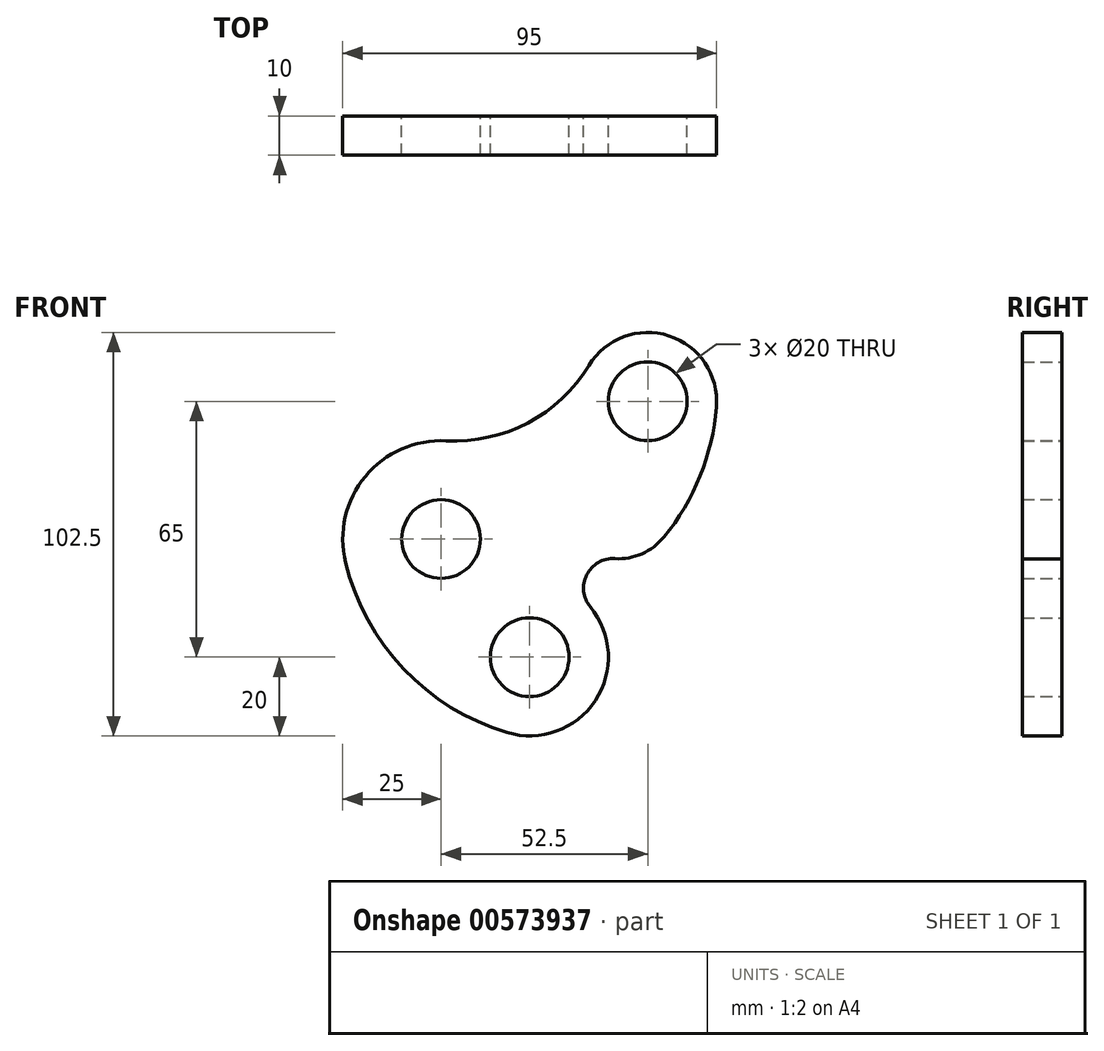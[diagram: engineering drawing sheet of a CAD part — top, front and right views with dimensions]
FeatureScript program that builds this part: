
annotation { "Feature Type Name" : "Feature", "Feature Type Description" : "" }
export const myFeature = defineFeature(function(context is Context, id is Id, definition is map)
    precondition{}
    {
        {
            var Q0;
            Q0=qCreatedBy(makeId("Front.planeOp"),FACE);
            var sketch = newSketch(context, id + "F0", { "sketchPlane" : qUnion([Q0])});
            skCircle(sketch, "E0", {"center": v(0, 0) * mm, "radius": 10 * mm});
            skCircle(sketch, "E1", {"center": v(22.5, -30) * mm, "radius": 10 * mm});
            skCircle(sketch, "E2", {"center": v(52.5, 35) * mm, "radius": 10 * mm});
            skArc(sketch, "E3", {"start": v(1.3, 24.97) * mm, "mid": v(-19.26, 15.94) * mm, "end": v(-24.28, -5.94) * mm});
            skArc(sketch, "E4", {"start": v(16.75, -49.16) * mm, "mid": v(39.17, -41.05) * mm, "end": v(37.9, -17.24) * mm});
            skArc(sketch, "E5", {"start": v(1.3, 24.97) * mm, "mid": v(22.07, 29.54) * mm, "end": v(37.55, 44.1) * mm});
            skArc(sketch, "E6", {"start": v(56.62, 0.51) * mm, "mid": v(65.8, 16.03) * mm, "end": v(69.94, 33.58) * mm});
            skArc(sketch, "E7", {"start": v(-24.28, -5.94) * mm, "mid": v(-9.51, -33) * mm, "end": v(16.75, -49.16) * mm});
            skArc(sketch, "E8", {"start": v(44.12, -4.97) * mm, "mid": v(37, -9.07) * mm, "end": v(37.9, -17.24) * mm});
            skArc(sketch, "E9", {"start": v(44.12, -4.97) * mm, "mid": v(51.03, -3.73) * mm, "end": v(56.62, 0.51) * mm});
            skArc(sketch, "E10.trimOffspring", {"start": v(69.94, 33.58) * mm, "mid": v(57.9, 51.64) * mm, "end": v(37.55, 44.1) * mm});
            skSolve(sketch);
        }
        {
            var Q0;
            Q0 = qSketchRegion(id + "F0", true);
            extrude(context, id + "F1", {"entities" : qUnion([Q0]), "depth" : 10 * mm, "offsetDistance" : 25 * mm});
        }
    });
